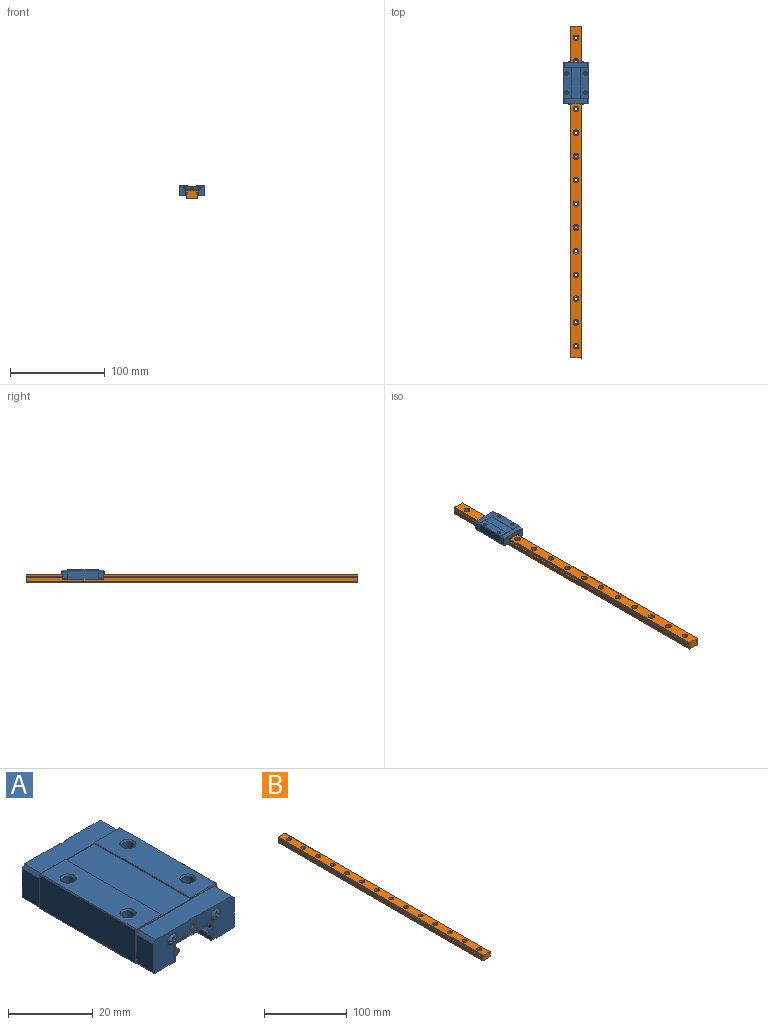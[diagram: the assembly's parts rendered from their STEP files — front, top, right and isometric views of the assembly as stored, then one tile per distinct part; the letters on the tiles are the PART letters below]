
ASSEMBLY  parts=2 mates=1
PART A: 286 faces, bbox 27.1x45.4x10.1 mm
  f0: plane 8.2x0.93mm, normal (0,-1,0), area 1.9mm2, adj f37,f39,f44,f244,f267
  f1: plane 8.2x0.93mm, normal (0,1,0), area 1.9mm2, adj f68,f70,f72,f141,f163
  f2: plane 3x3mm, normal (0,0,1), area 7.1mm2, adj f4
  f3: plane 3x3mm, normal (0,0,1), area 7.1mm2, adj f5
  f4: cylinder r=1.5mm len=5.45mm, axis (0,0,1), area 51.4mm2, adj f2,f31
  f5: cylinder r=1.5mm len=5.45mm, axis (0,0,1), area 51.4mm2, adj f3,f40
  f6: plane 8.2x0.93mm, normal (0,-1,0), area 1.9mm2, adj f26,f30,f33,f244,f266
  f7: plane 1.37x0.22mm, normal (0.71,-0.71,0), area 0.3mm2, adj f8,f50,f51,f186
  f8: cone r=1mm half-angle=45deg, axis (0,-1,0), area 1.1mm2, adj f7,f9,f10,f186
  f9: cylinder r=1mm len=32mm, axis (0,1,0), area 120.6mm2, adj f8,f11,f51,f59
  f10: plane 1.77x0.22mm, normal (0.71,-0.71,0), area 0.4mm2, adj f8,f11,f12,f186
  f11: plane 32x1.55mm, normal (1,0,0), area 49.6mm2, adj f9,f10,f13,f60
  f12: plane 12.4x0.2mm, normal (0,-0.71,-0.71), area 3.5mm2, adj f10,f13,f14,f186
  f13: plane 32x12mm, normal (0,0,-1), area 384mm2, adj f11,f12,f15,f61
  f14: plane 1.77x0.22mm, normal (-0.71,-0.71,0), area 0.4mm2, adj f12,f15,f16,f186
  f15: plane 32x1.55mm, normal (-1,0,0), area 49.6mm2, adj f13,f14,f17,f62
  f16: cone r=1.2mm half-angle=45deg, axis (0,-1,0), area 1.1mm2, adj f14,f17,f18,f186
  f17: cylinder r=1mm len=32mm, axis (0,1,0), area 120.6mm2, adj f15,f16,f19,f63
  f18: plane 1.37x0.22mm, normal (-0.71,-0.71,0), area 0.3mm2, adj f16,f19,f20,f186
  f19: plane 32x1.35mm, normal (-1,0,0), area 43.2mm2, adj f17,f18,f21,f64
  f20: plane 0.2x0.2mm, normal (-0.58,-0.58,-0.58), area 0mm2, adj f18,f21,f22
  f21: plane 32x0.2mm, normal (-0.71,0,-0.71), area 9.1mm2, adj f19,f20,f23,f65
  f22: plane 7.1x0.2mm, normal (0,-0.71,-0.71), area 2mm2, adj f20,f23,f24,f186
  f23: plane 32x7.1mm, normal (0,0,-1), area 227.2mm2, adj f21,f22,f25,f66
  f24: plane 0.2x0.2mm, normal (0.58,-0.58,-0.58), area 0mm2, adj f22,f25,f26
  f25: plane 32x0.2mm, normal (0.71,0,-0.71), area 9.1mm2, adj f23,f24,f27,f67
  f26: plane 9.6x0.2mm, normal (0.71,-0.71,0), area 2.7mm2, adj f6,f24,f27,f28,f185
  f27: plane 32x9.6mm, normal (1,0,0), area 307.2mm2, adj f25,f26,f29,f68
  f28: plane 0.2x0.2mm, normal (0.58,-0.58,0.58), area 0mm2, adj f26,f29,f30
  f29: plane 32x0.2mm, normal (0.71,0,0.71), area 9.1mm2, adj f27,f28,f32,f69
  f30: plane 8.4x0.2mm, normal (0,-0.71,0.71), area 2.3mm2, adj f6,f28,f32,f33
  f31: cone r=1.5mm half-angle=45deg, axis (0,0,1), area 6mm2, adj f4,f32
  f32: plane 32x8.4mm, normal (0,0,1), area 246.1mm2, adj f29,f30,f31,f34,f70,f71
  f33: plane 0.6x0.2mm, normal (-0.71,-0.71,0), area 0.1mm2, adj f6,f30,f34,f35,f184
  f34: plane 32x0.4mm, normal (-1,0,0), area 12.8mm2, adj f32,f33,f36,f72
  f35: plane 10.2x0.2mm, normal (0,-0.71,0.71), area 2.8mm2, adj f33,f36,f37,f184
  f36: plane 32x9.8mm, normal (0,0,1), area 313.6mm2, adj f34,f35,f38,f73
  f37: plane 0.6x0.2mm, normal (0.71,-0.71,0), area 0.1mm2, adj f0,f35,f38,f39,f184
  f38: plane 32x0.4mm, normal (1,0,0), area 12.8mm2, adj f36,f37,f41,f74
  f39: plane 8.4x0.2mm, normal (0,-0.71,0.71), area 2.3mm2, adj f0,f37,f41,f42
  f40: cone r=1.5mm half-angle=45deg, axis (0,0,1), area 6mm2, adj f5,f41
  f41: plane 32x8.4mm, normal (0,0,1), area 246.1mm2, adj f38,f39,f40,f43,f75,f76
  f42: plane 0.2x0.2mm, normal (-0.58,-0.58,0.58), area 0mm2, adj f39,f43,f44
  f43: plane 32x0.2mm, normal (-0.71,0,0.71), area 9.1mm2, adj f41,f42,f45,f77
  f44: plane 9.6x0.2mm, normal (-0.71,-0.71,0), area 2.7mm2, adj f0,f42,f45,f46,f187
  f45: plane 32x9.6mm, normal (-1,0,0), area 307.2mm2, adj f43,f44,f47,f78
  f46: plane 0.2x0.2mm, normal (-0.58,-0.58,-0.58), area 0mm2, adj f44,f47,f48
  f47: plane 32x0.2mm, normal (-0.71,0,-0.71), area 9.1mm2, adj f45,f46,f49,f79
  f48: plane 7.1x0.2mm, normal (0,-0.71,-0.71), area 2mm2, adj f46,f49,f50,f186
  f49: plane 32x7.1mm, normal (0,0,-1), area 227.2mm2, adj f47,f48,f52,f80
  f50: plane 0.2x0.2mm, normal (0.58,-0.58,-0.58), area 0mm2, adj f7,f48,f52
  f51: plane 32x1.35mm, normal (1,0,0), area 43.2mm2, adj f7,f9,f52,f58
  f52: plane 32x0.2mm, normal (0.71,0,-0.71), area 9.1mm2, adj f49,f50,f51,f81
  f53: plane 3x3mm, normal (0,0,1), area 7.1mm2, adj f55
  f54: plane 3x3mm, normal (0,0,1), area 7.1mm2, adj f56
  f55: cylinder r=1.5mm len=5.45mm, axis (0,0,1), area 51.4mm2, adj f53,f71
  f56: cylinder r=1.5mm len=5.45mm, axis (0,0,1), area 51.4mm2, adj f54,f76
  f57: plane 8.2x0.93mm, normal (0,1,0), area 1.9mm2, adj f74,f75,f78,f141,f164
  f58: plane 1.37x0.22mm, normal (0.71,0.71,0), area 0.3mm2, adj f51,f59,f81,f84
  f59: cone r=1mm half-angle=45deg, axis (0,1,0), area 1.1mm2, adj f9,f58,f60,f84
  f60: plane 1.77x0.22mm, normal (0.71,0.71,0), area 0.4mm2, adj f11,f59,f61,f84
  f61: plane 12.4x0.2mm, normal (0,0.71,-0.71), area 3.5mm2, adj f13,f60,f62,f84
  f62: plane 1.77x0.22mm, normal (-0.71,0.71,0), area 0.4mm2, adj f15,f61,f63,f84
  f63: cone r=1.2mm half-angle=45deg, axis (0,1,0), area 1.1mm2, adj f17,f62,f64,f84
  f64: plane 1.37x0.22mm, normal (-0.71,0.71,0), area 0.3mm2, adj f19,f63,f65,f84
  f65: plane 0.2x0.2mm, normal (-0.58,0.58,-0.58), area 0mm2, adj f21,f64,f66
  f66: plane 7.1x0.2mm, normal (0,0.71,-0.71), area 2mm2, adj f23,f65,f67,f84
  f67: plane 0.2x0.2mm, normal (0.58,0.58,-0.58), area 0mm2, adj f25,f66,f68
  f68: plane 9.6x0.2mm, normal (0.71,0.71,0), area 2.7mm2, adj f1,f27,f67,f69,f182
  f69: plane 0.2x0.2mm, normal (0.58,0.58,0.58), area 0mm2, adj f29,f68,f70
  f70: plane 8.4x0.2mm, normal (0,0.71,0.71), area 2.3mm2, adj f1,f32,f69,f72
  f71: cone r=1.5mm half-angle=45deg, axis (0,0,1), area 6mm2, adj f32,f55
  f72: plane 0.6x0.2mm, normal (-0.71,0.71,0), area 0.1mm2, adj f1,f34,f70,f73,f82
  f73: plane 10.2x0.2mm, normal (0,0.71,0.71), area 2.8mm2, adj f36,f72,f74,f82
  f74: plane 0.6x0.2mm, normal (0.71,0.71,0), area 0.1mm2, adj f38,f57,f73,f75,f82
  f75: plane 8.4x0.2mm, normal (0,0.71,0.71), area 2.3mm2, adj f41,f57,f74,f77
  f76: cone r=1.5mm half-angle=45deg, axis (0,0,1), area 6mm2, adj f41,f56
  f77: plane 0.2x0.2mm, normal (-0.58,0.58,0.58), area 0mm2, adj f43,f75,f78
  f78: plane 9.6x0.2mm, normal (-0.71,0.71,0), area 2.7mm2, adj f45,f57,f77,f79,f83
  f79: plane 0.2x0.2mm, normal (-0.58,0.58,-0.58), area 0mm2, adj f47,f78,f80
  f80: plane 7.1x0.2mm, normal (0,0.71,-0.71), area 2mm2, adj f49,f79,f81,f84
  f81: plane 0.2x0.2mm, normal (0.58,0.58,-0.58), area 0mm2, adj f52,f58,f80
  f82: plane 10.2x0.2mm, normal (0,-1,0), area 2mm2, adj f72,f73,f74,f141
  f83: plane 8.67x0.2mm, normal (0,-1,0), area 1.7mm2, adj f78,f146,f164,f165
  f84: plane 26.6x5.2mm, normal (0,-1,0), area 8mm2, adj f58,f59,f60,f61,f62,f63,f64,f66
  f85: sphere r=1.65mm, area 14.5mm2, adj f86,f87,f90,f92,f93,f96,f98,f99
  f86: plane 0.66x0.4mm, normal (0,0,-1), area 0.2mm2, adj f85,f87,f89,f90
  f87: plane 0.77x0.69mm, normal (-1,0,0), area 0.4mm2, adj f85,f86,f88,f108
  f88: plane 1.08x0.89mm, normal (-0.95,0.33,0), area 0.7mm2, adj f87,f89,f91,f109
  f89: plane 0.89x0.61mm, normal (0,0.33,-0.95), area 0.3mm2, adj f86,f88,f91
  f90: plane 0.77x0.69mm, normal (1,0,0), area 0.4mm2, adj f85,f86,f91,f96
  f91: plane 1.08x0.89mm, normal (0.95,0.33,0), area 0.7mm2, adj f88,f89,f90,f97
  f92: plane 0.61x0.35mm, normal (1,0,0), area 0.2mm2, adj f85,f93,f94,f96
  f93: plane 0.8x0.73mm, normal (0,0,1), area 0.4mm2, adj f85,f92,f95,f102
  f94: plane 0.89x0.61mm, normal (0.95,0.33,0), area 0.3mm2, adj f92,f95,f97
  f95: plane 1.08x0.89mm, normal (0,0.33,0.95), area 0.7mm2, adj f93,f94,f97,f103
  f96: plane 0.8x0.73mm, normal (0,0,-1), area 0.4mm2, adj f85,f90,f92,f97
  f97: plane 1.08x0.89mm, normal (0,0.33,-0.95), area 0.7mm2, adj f91,f94,f95,f96
  f98: plane 0.66x0.4mm, normal (0,0,1), area 0.2mm2, adj f85,f99,f100,f102
  f99: plane 0.77x0.69mm, normal (-1,0,0), area 0.4mm2, adj f85,f98,f101,f105
  f100: plane 0.89x0.61mm, normal (0,0.33,0.95), area 0.3mm2, adj f98,f101,f103
  f101: plane 1.08x0.89mm, normal (-0.95,0.33,0), area 0.7mm2, adj f99,f100,f103,f106
  f102: plane 0.77x0.69mm, normal (1,0,0), area 0.4mm2, adj f85,f93,f98,f103
  f103: plane 1.08x0.89mm, normal (0.95,0.33,0), area 0.7mm2, adj f95,f100,f101,f102
  f104: plane 0.61x0.35mm, normal (-1,0,0), area 0.2mm2, adj f85,f105,f107,f108
  f105: plane 0.8x0.73mm, normal (0,0,1), area 0.4mm2, adj f85,f99,f104,f106
  f106: plane 1.08x0.89mm, normal (0,0.33,0.95), area 0.7mm2, adj f101,f105,f107,f109
  f107: plane 0.89x0.61mm, normal (-0.95,0.33,0), area 0.3mm2, adj f104,f106,f109
  f108: plane 0.8x0.73mm, normal (0,0,-1), area 0.4mm2, adj f85,f87,f104,f109
  f109: plane 1.08x0.89mm, normal (0,0.33,-0.95), area 0.7mm2, adj f88,f106,f107,f108
  f110: sphere r=1.65mm, area 14.5mm2, adj f111,f112,f113,f117,f118,f120,f123,f124
  f111: plane 0.61x0.35mm, normal (-1,0,0), area 0.2mm2, adj f110,f112,f113,f114
  f112: plane 0.8x0.73mm, normal (0,0,-1), area 0.4mm2, adj f110,f111,f115,f125
  f113: plane 0.8x0.73mm, normal (0,0,1), area 0.4mm2, adj f110,f111,f116,f120
  f114: plane 0.89x0.61mm, normal (-0.95,0.33,0), area 0.3mm2, adj f111,f115,f116
  f115: plane 1.08x0.89mm, normal (0,0.33,-0.95), area 0.7mm2, adj f112,f114,f116,f128
  f116: plane 1.08x0.89mm, normal (0,0.33,0.95), area 0.7mm2, adj f113,f114,f115,f122
  f117: plane 0.66x0.4mm, normal (0,0,1), area 0.2mm2, adj f110,f118,f119,f120
  f118: plane 0.77x0.69mm, normal (1,0,0), area 0.4mm2, adj f110,f117,f121,f132
  f119: plane 0.89x0.61mm, normal (0,0.33,0.95), area 0.3mm2, adj f117,f121,f122
  f120: plane 0.77x0.69mm, normal (-1,0,0), area 0.4mm2, adj f110,f113,f117,f122
  f121: plane 1.08x0.89mm, normal (0.95,0.33,0), area 0.7mm2, adj f118,f119,f122,f134
  f122: plane 1.08x0.89mm, normal (-0.95,0.33,0), area 0.7mm2, adj f116,f119,f120,f121
  f123: plane 0.66x0.4mm, normal (0,0,-1), area 0.2mm2, adj f110,f124,f125,f126
  f124: plane 0.77x0.69mm, normal (1,0,0), area 0.4mm2, adj f110,f123,f127,f130
  f125: plane 0.77x0.69mm, normal (-1,0,0), area 0.4mm2, adj f110,f112,f123,f128
  f126: plane 0.89x0.61mm, normal (0,0.33,-0.95), area 0.3mm2, adj f123,f127,f128
  f127: plane 1.08x0.89mm, normal (0.95,0.33,0), area 0.7mm2, adj f124,f126,f128,f133
  f128: plane 1.08x0.89mm, normal (-0.95,0.33,0), area 0.7mm2, adj f115,f125,f126,f127
  f129: plane 0.61x0.35mm, normal (1,0,0), area 0.2mm2, adj f110,f130,f131,f132
  f130: plane 0.8x0.73mm, normal (0,0,-1), area 0.4mm2, adj f110,f124,f129,f133
  f131: plane 0.89x0.61mm, normal (0.95,0.33,0), area 0.3mm2, adj f129,f133,f134
  f132: plane 0.8x0.73mm, normal (0,0,1), area 0.4mm2, adj f110,f118,f129,f134
  f133: plane 1.08x0.89mm, normal (0,0.33,-0.95), area 0.7mm2, adj f127,f130,f131,f134
  f134: plane 1.08x0.89mm, normal (0,0.33,0.95), area 0.7mm2, adj f121,f131,f132,f133
  f135: plane 2.67x2mm, normal (0,-1,0), area 3.5mm2, adj f156,f157,f158,f159,f160,f180
  f136: plane 2.67x2mm, normal (0,-1,0), area 3.5mm2, adj f148,f149,f150,f151,f152,f181
  f137: plane 12.41x9.6mm, normal (0,1,0), area 77.5mm2, adj f139,f141,f142,f146,f164,f165,f169,f170
  f138: plane 12.41x9.6mm, normal (0,1,0), area 77.5mm2, adj f140,f141,f143,f162,f163,f166,f172,f173
  f139: plane 7.1x5.7mm, normal (0,0,-1), area 40.4mm2, adj f84,f137,f145,f147,f165,f167,f169,f177
  f140: plane 7.1x5.7mm, normal (0,0,-1), area 40.4mm2, adj f84,f138,f145,f161,f166,f174,f175,f178
  f141: plane 25.14x5.7mm, normal (0,0,1), area 142.9mm2, adj f1,f57,f82,f137,f138,f163,f164,f168
  f142: cylinder r=1.65mm len=3.3mm, axis (0,-1,0), area 9.1mm2, adj f110,f137,f167,f168,f169,f170
  f143: cylinder r=1.65mm len=3.3mm, axis (0,-1,0), area 9.1mm2, adj f85,f138,f168,f173,f174,f178
  f144: cylinder r=0.75mm len=1.5mm, axis (0,-1,0), area 3.3mm2, adj f168,f179
  f145: plane 12.8x5.36mm, normal (0,1,0), area 11.3mm2, adj f139,f140,f147,f148,f149,f150,f151,f152
  f146: plane 8.27x5.7mm, normal (-1,0,0), area 47.1mm2, adj f83,f137,f164,f165
  f147: plane 5.7x1.55mm, normal (1,0,0), area 8.8mm2, adj f84,f139,f145,f148,f181
  f148: cylinder r=1mm len=0.9mm, axis (0,-1,0), area 0.9mm2, adj f136,f145,f147,f149
  f149: plane 0.9x0.71mm, normal (0,0,-1), area 0.6mm2, adj f136,f145,f148,f150
  f150: plane 0.9x0.6mm, normal (1,0,0), area 0.5mm2, adj f136,f145,f149,f151
  f151: plane 0.9x0.71mm, normal (0,0,1), area 0.6mm2, adj f136,f145,f150,f152
  f152: cylinder r=1mm len=0.9mm, axis (0,-1,0), area 0.9mm2, adj f136,f145,f151,f153
  f153: plane 5.7x1.55mm, normal (1,0,0), area 8.8mm2, adj f84,f145,f152,f154,f181
  f154: plane 12x5.7mm, normal (0,0,-1), area 68.4mm2, adj f84,f145,f153,f155
  f155: plane 5.7x1.55mm, normal (-1,0,0), area 8.8mm2, adj f84,f145,f154,f156,f180
  f156: cylinder r=1mm len=0.9mm, axis (0,-1,0), area 0.9mm2, adj f135,f145,f155,f157
  f157: plane 0.9x0.71mm, normal (0,0,1), area 0.6mm2, adj f135,f145,f156,f158
  f158: plane 0.9x0.6mm, normal (-1,0,0), area 0.5mm2, adj f135,f145,f157,f159
  f159: plane 0.9x0.71mm, normal (0,0,-1), area 0.6mm2, adj f135,f145,f158,f160
  f160: cylinder r=1mm len=0.9mm, axis (0,-1,0), area 0.9mm2, adj f135,f145,f159,f161
  f161: plane 5.7x1.55mm, normal (-1,0,0), area 8.8mm2, adj f84,f140,f145,f160,f180
  f162: plane 8.27x5.7mm, normal (1,0,0), area 47.1mm2, adj f138,f163,f166,f182
  f163: plane 5.7x0.93mm, normal (0.71,0,0.71), area 7.5mm2, adj f1,f138,f141,f162,f182
  f164: plane 5.7x0.93mm, normal (-0.71,0,0.71), area 7.5mm2, adj f57,f83,f137,f141,f146
  f165: plane 5.7x0.4mm, normal (-0.71,0,-0.71), area 3.2mm2, adj f83,f84,f137,f139,f146
  f166: plane 5.7x0.4mm, normal (0.71,0,-0.71), area 3.2mm2, adj f84,f138,f140,f162,f182
  f167: plane 5.36x0.4mm, normal (0,1,0), area 2.1mm2, adj f139,f142,f169,f177
  f168: plane 12.8x4.24mm, normal (0,1,0), area 11.5mm2, adj f141,f142,f143,f144,f170,f171,f172,f173
  f169: plane 5.2x0.2mm, normal (1,0,0), area 1mm2, adj f137,f139,f142,f167
  f170: plane 4.83x0.2mm, normal (0,0,-1), area 1mm2, adj f137,f142,f168,f171
  f171: plane 3.84x0.2mm, normal (1,0,0), area 0.8mm2, adj f137,f141,f168,f170
  f172: plane 3.84x0.2mm, normal (-1,0,0), area 0.8mm2, adj f138,f141,f168,f173
  f173: plane 4.83x0.2mm, normal (0,0,-1), area 1mm2, adj f138,f143,f168,f172
  f174: plane 5.2x0.2mm, normal (-1,0,0), area 1mm2, adj f138,f140,f143,f178
  f175: plane 5.36x0.2mm, normal (1,0,0), area 1.1mm2, adj f140,f145,f176,f178
  f176: plane 12.8x0.2mm, normal (0,0,1), area 2.6mm2, adj f145,f168,f175,f177
  f177: plane 5.36x0.2mm, normal (-1,0,0), area 1.1mm2, adj f139,f145,f167,f176
  f178: plane 5.36x0.4mm, normal (0,1,0), area 2.1mm2, adj f140,f143,f174,f175
  f179: cylinder r=0.75mm len=4.8mm, axis (0,-1,0), area 22.6mm2, adj f144,f183
  f180: cylinder r=1mm len=4.8mm, axis (0,-1,0), area 18.1mm2, adj f84,f135,f155,f161
  f181: cylinder r=1mm len=4.8mm, axis (0,-1,0), area 18.1mm2, adj f84,f136,f147,f153
  f182: plane 8.67x0.2mm, normal (0,-1,0), area 1.7mm2, adj f68,f162,f163,f166
  f183: plane 1.5x1.5mm, normal (0,1,0), area 1.8mm2, adj f179
  f184: plane 10.2x0.2mm, normal (0,1,0), area 2mm2, adj f33,f35,f37,f244
  f185: plane 8.67x0.2mm, normal (0,1,0), area 1.7mm2, adj f26,f265,f266,f269
  f186: plane 26.6x5.2mm, normal (0,1,0), area 8mm2, adj f7,f8,f10,f12,f14,f16,f18,f22
  f187: plane 8.67x0.2mm, normal (0,1,0), area 1.7mm2, adj f44,f249,f267,f268
  f188: sphere r=1.65mm, area 14.5mm2, adj f189,f190,f193,f195,f196,f199,f201,f202
  f189: plane 0.66x0.4mm, normal (0,0,-1), area 0.2mm2, adj f188,f190,f192,f193
  f190: plane 0.77x0.69mm, normal (-1,0,0), area 0.4mm2, adj f188,f189,f191,f211
  f191: plane 1.08x0.89mm, normal (-0.95,-0.33,0), area 0.7mm2, adj f190,f192,f194,f212
  f192: plane 0.89x0.61mm, normal (0,-0.33,-0.95), area 0.3mm2, adj f189,f191,f194
  f193: plane 0.77x0.69mm, normal (1,0,0), area 0.4mm2, adj f188,f189,f194,f199
  f194: plane 1.08x0.89mm, normal (0.95,-0.33,0), area 0.7mm2, adj f191,f192,f193,f200
  f195: plane 0.61x0.35mm, normal (1,0,0), area 0.2mm2, adj f188,f196,f197,f199
  f196: plane 0.8x0.73mm, normal (0,0,1), area 0.4mm2, adj f188,f195,f198,f205
  f197: plane 0.89x0.61mm, normal (0.95,-0.33,0), area 0.3mm2, adj f195,f198,f200
  f198: plane 1.08x0.89mm, normal (0,-0.33,0.95), area 0.7mm2, adj f196,f197,f200,f206
  f199: plane 0.8x0.73mm, normal (0,0,-1), area 0.4mm2, adj f188,f193,f195,f200
  f200: plane 1.08x0.89mm, normal (0,-0.33,-0.95), area 0.7mm2, adj f194,f197,f198,f199
  f201: plane 0.66x0.4mm, normal (0,0,1), area 0.2mm2, adj f188,f202,f203,f205
  f202: plane 0.77x0.69mm, normal (-1,0,0), area 0.4mm2, adj f188,f201,f204,f208
  f203: plane 0.89x0.61mm, normal (0,-0.33,0.95), area 0.3mm2, adj f201,f204,f206
  f204: plane 1.08x0.89mm, normal (-0.95,-0.33,0), area 0.7mm2, adj f202,f203,f206,f209
  f205: plane 0.77x0.69mm, normal (1,0,0), area 0.4mm2, adj f188,f196,f201,f206
  f206: plane 1.08x0.89mm, normal (0.95,-0.33,0), area 0.7mm2, adj f198,f203,f204,f205
  f207: plane 0.61x0.35mm, normal (-1,0,0), area 0.2mm2, adj f188,f208,f210,f211
  f208: plane 0.8x0.73mm, normal (0,0,1), area 0.4mm2, adj f188,f202,f207,f209
  f209: plane 1.08x0.89mm, normal (0,-0.33,0.95), area 0.7mm2, adj f204,f208,f210,f212
  f210: plane 0.89x0.61mm, normal (-0.95,-0.33,0), area 0.3mm2, adj f207,f209,f212
  f211: plane 0.8x0.73mm, normal (0,0,-1), area 0.4mm2, adj f188,f190,f207,f212
  f212: plane 1.08x0.89mm, normal (0,-0.33,-0.95), area 0.7mm2, adj f191,f209,f210,f211
  f213: sphere r=1.65mm, area 14.5mm2, adj f214,f215,f216,f220,f221,f223,f226,f227
  f214: plane 0.61x0.35mm, normal (-1,0,0), area 0.2mm2, adj f213,f215,f216,f217
  f215: plane 0.8x0.73mm, normal (0,0,-1), area 0.4mm2, adj f213,f214,f218,f228
  f216: plane 0.8x0.73mm, normal (0,0,1), area 0.4mm2, adj f213,f214,f219,f223
  f217: plane 0.89x0.61mm, normal (-0.95,-0.33,0), area 0.3mm2, adj f214,f218,f219
  f218: plane 1.08x0.89mm, normal (0,-0.33,-0.95), area 0.7mm2, adj f215,f217,f219,f231
  f219: plane 1.08x0.89mm, normal (0,-0.33,0.95), area 0.7mm2, adj f216,f217,f218,f225
  f220: plane 0.66x0.4mm, normal (0,0,1), area 0.2mm2, adj f213,f221,f222,f223
  f221: plane 0.77x0.69mm, normal (1,0,0), area 0.4mm2, adj f213,f220,f224,f235
  f222: plane 0.89x0.61mm, normal (0,-0.33,0.95), area 0.3mm2, adj f220,f224,f225
  f223: plane 0.77x0.69mm, normal (-1,0,0), area 0.4mm2, adj f213,f216,f220,f225
  f224: plane 1.08x0.89mm, normal (0.95,-0.33,0), area 0.7mm2, adj f221,f222,f225,f237
  f225: plane 1.08x0.89mm, normal (-0.95,-0.33,0), area 0.7mm2, adj f219,f222,f223,f224
  f226: plane 0.66x0.4mm, normal (0,0,-1), area 0.2mm2, adj f213,f227,f228,f229
  f227: plane 0.77x0.69mm, normal (1,0,0), area 0.4mm2, adj f213,f226,f230,f233
  f228: plane 0.77x0.69mm, normal (-1,0,0), area 0.4mm2, adj f213,f215,f226,f231
  f229: plane 0.89x0.61mm, normal (0,-0.33,-0.95), area 0.3mm2, adj f226,f230,f231
  f230: plane 1.08x0.89mm, normal (0.95,-0.33,0), area 0.7mm2, adj f227,f229,f231,f236
  f231: plane 1.08x0.89mm, normal (-0.95,-0.33,0), area 0.7mm2, adj f218,f228,f229,f230
  f232: plane 0.61x0.35mm, normal (1,0,0), area 0.2mm2, adj f213,f233,f234,f235
  f233: plane 0.8x0.73mm, normal (0,0,-1), area 0.4mm2, adj f213,f227,f232,f236
  f234: plane 0.89x0.61mm, normal (0.95,-0.33,0), area 0.3mm2, adj f232,f236,f237
  f235: plane 0.8x0.73mm, normal (0,0,1), area 0.4mm2, adj f213,f221,f232,f237
  f236: plane 1.08x0.89mm, normal (0,-0.33,-0.95), area 0.7mm2, adj f230,f233,f234,f237
  f237: plane 1.08x0.89mm, normal (0,-0.33,0.95), area 0.7mm2, adj f224,f234,f235,f236
  f238: plane 2.67x2mm, normal (0,1,0), area 3.5mm2, adj f251,f252,f253,f254,f255,f284
  f239: plane 2.67x2mm, normal (0,1,0), area 3.5mm2, adj f259,f260,f261,f262,f263,f283
  f240: plane 12.41x9.6mm, normal (0,-1,0), area 77.5mm2, adj f242,f244,f245,f249,f267,f268,f272,f273
  f241: plane 12.41x9.6mm, normal (0,-1,0), area 77.5mm2, adj f243,f244,f246,f265,f266,f269,f275,f276
  f242: plane 7.1x5.7mm, normal (0,0,-1), area 40.4mm2, adj f186,f240,f248,f250,f268,f270,f272,f280
  f243: plane 7.1x5.7mm, normal (0,0,-1), area 40.4mm2, adj f186,f241,f248,f264,f269,f277,f278,f281
  f244: plane 25.14x5.7mm, normal (0,0,1), area 142.9mm2, adj f0,f6,f184,f240,f241,f266,f267,f271
  f245: cylinder r=1.65mm len=3.3mm, axis (0,1,0), area 9.1mm2, adj f213,f240,f270,f271,f272,f273
  f246: cylinder r=1.65mm len=3.3mm, axis (0,1,0), area 9.1mm2, adj f188,f241,f271,f276,f277,f281
  f247: cylinder r=0.75mm len=1.5mm, axis (0,1,0), area 3.3mm2, adj f271,f282
  f248: plane 12.8x5.36mm, normal (0,-1,0), area 11.3mm2, adj f242,f243,f250,f251,f252,f253,f254,f255
  f249: plane 8.27x5.7mm, normal (-1,0,0), area 47.1mm2, adj f187,f240,f267,f268
  f250: plane 5.7x1.55mm, normal (1,0,0), area 8.8mm2, adj f186,f242,f248,f251,f284
  f251: cylinder r=1mm len=0.9mm, axis (0,1,0), area 0.9mm2, adj f238,f248,f250,f252
  f252: plane 0.9x0.71mm, normal (0,0,-1), area 0.6mm2, adj f238,f248,f251,f253
  f253: plane 0.9x0.6mm, normal (1,0,0), area 0.5mm2, adj f238,f248,f252,f254
  f254: plane 0.9x0.71mm, normal (0,0,1), area 0.6mm2, adj f238,f248,f253,f255
  f255: cylinder r=1mm len=0.9mm, axis (0,1,0), area 0.9mm2, adj f238,f248,f254,f256
  f256: plane 5.7x1.55mm, normal (1,0,0), area 8.8mm2, adj f186,f248,f255,f257,f284
  f257: plane 12x5.7mm, normal (0,0,-1), area 68.4mm2, adj f186,f248,f256,f258
  f258: plane 5.7x1.55mm, normal (-1,0,0), area 8.8mm2, adj f186,f248,f257,f259,f283
  f259: cylinder r=1mm len=0.9mm, axis (0,1,0), area 0.9mm2, adj f239,f248,f258,f260
  f260: plane 0.9x0.71mm, normal (0,0,1), area 0.6mm2, adj f239,f248,f259,f261
  f261: plane 0.9x0.6mm, normal (-1,0,0), area 0.5mm2, adj f239,f248,f260,f262
  f262: plane 0.9x0.71mm, normal (0,0,-1), area 0.6mm2, adj f239,f248,f261,f263
  f263: cylinder r=1mm len=0.9mm, axis (0,1,0), area 0.9mm2, adj f239,f248,f262,f264
  f264: plane 5.7x1.55mm, normal (-1,0,0), area 8.8mm2, adj f186,f243,f248,f263,f283
  f265: plane 8.27x5.7mm, normal (1,0,0), area 47.1mm2, adj f185,f241,f266,f269
  f266: plane 5.7x0.93mm, normal (0.71,0,0.71), area 7.5mm2, adj f6,f185,f241,f244,f265
  f267: plane 5.7x0.93mm, normal (-0.71,0,0.71), area 7.5mm2, adj f0,f187,f240,f244,f249
  f268: plane 5.7x0.4mm, normal (-0.71,0,-0.71), area 3.2mm2, adj f186,f187,f240,f242,f249
  f269: plane 5.7x0.4mm, normal (0.71,0,-0.71), area 3.2mm2, adj f185,f186,f241,f243,f265
  f270: plane 5.36x0.4mm, normal (0,-1,0), area 2.1mm2, adj f242,f245,f272,f280
  f271: plane 12.8x4.24mm, normal (0,-1,0), area 11.5mm2, adj f244,f245,f246,f247,f273,f274,f275,f276
  f272: plane 5.2x0.2mm, normal (1,0,0), area 1mm2, adj f240,f242,f245,f270
  f273: plane 4.83x0.2mm, normal (0,0,-1), area 1mm2, adj f240,f245,f271,f274
  f274: plane 3.84x0.2mm, normal (1,0,0), area 0.8mm2, adj f240,f244,f271,f273
  f275: plane 3.84x0.2mm, normal (-1,0,0), area 0.8mm2, adj f241,f244,f271,f276
  f276: plane 4.83x0.2mm, normal (0,0,-1), area 1mm2, adj f241,f246,f271,f275
  f277: plane 5.2x0.2mm, normal (-1,0,0), area 1mm2, adj f241,f243,f246,f281
  f278: plane 5.36x0.2mm, normal (1,0,0), area 1.1mm2, adj f243,f248,f279,f281
  f279: plane 12.8x0.2mm, normal (0,0,1), area 2.6mm2, adj f248,f271,f278,f280
  f280: plane 5.36x0.2mm, normal (-1,0,0), area 1.1mm2, adj f242,f248,f270,f279
  f281: plane 5.36x0.4mm, normal (0,-1,0), area 2.1mm2, adj f243,f246,f277,f278
  f282: cylinder r=0.75mm len=4.8mm, axis (0,1,0), area 22.6mm2, adj f247,f285
  f283: cylinder r=1mm len=4.8mm, axis (0,1,0), area 18.1mm2, adj f186,f239,f258,f264
  f284: cylinder r=1mm len=4.8mm, axis (0,1,0), area 18.1mm2, adj f186,f238,f250,f256
  f285: plane 1.5x1.5mm, normal (0,-1,0), area 1.8mm2, adj f282
PART B: 64 faces, bbox 12x350x8 mm
  f0: plane 350x1.25mm, normal (-1,0,0), area 437.1mm2, adj f1,f19,f20,f51
  f1: cylinder r=1mm len=350mm, axis (0,1,0), area 333.8mm2, adj f0,f2,f20,f51
  f2: plane 350x0.71mm, normal (0,0,-1), area 248.9mm2, adj f1,f3,f20,f51
  f3: plane 350x0.6mm, normal (-1,0,0), area 208.6mm2, adj f2,f4,f20,f51
  f4: plane 350x0.71mm, normal (0,0,1), area 248.9mm2, adj f3,f5,f20,f51
  f5: cylinder r=1mm len=350mm, axis (0,1,0), area 333.8mm2, adj f4,f6,f20,f51
  f6: plane 350x4.25mm, normal (-1,0,0), area 1487.1mm2, adj f5,f7,f20,f51
  f7: plane 350x0.3mm, normal (-0.71,0,-0.71), area 148.5mm2, adj f6,f8,f20,f51
  f8: plane 350x11.4mm, normal (0,0,-1), area 3855.3mm2, adj f7,f9,f20,f23,f42,f43,f44,f45
  f9: plane 350x0.3mm, normal (0.71,0,-0.71), area 148.5mm2, adj f8,f10,f20,f51
  f10: plane 350x4.25mm, normal (1,0,0), area 1487.1mm2, adj f9,f11,f20,f51
  f11: cylinder r=1mm len=350mm, axis (0,1,0), area 333.8mm2, adj f10,f12,f20,f51
  f12: plane 350x0.71mm, normal (0,0,1), area 248.9mm2, adj f11,f13,f20,f51
  f13: plane 350x0.6mm, normal (1,0,0), area 208.6mm2, adj f12,f14,f20,f51
  f14: plane 350x0.71mm, normal (0,0,-1), area 248.9mm2, adj f13,f15,f20,f51
  f15: cylinder r=1mm len=350mm, axis (0,1,0), area 333.8mm2, adj f14,f16,f20,f51
  f16: plane 350x1.25mm, normal (1,0,0), area 437.1mm2, adj f15,f17,f20,f51
  f17: plane 350x0.3mm, normal (0.71,0,0.71), area 148.5mm2, adj f16,f18,f20,f51
  f18: plane 350x11.4mm, normal (0,0,1), area 3594.2mm2, adj f17,f19,f20,f21,f24,f27,f29,f31
  f19: plane 350x0.3mm, normal (-0.71,0,0.71), area 148.5mm2, adj f0,f18,f20,f51
  f20: plane 12x8mm, normal (0,1,0), area 93.1mm2, adj f0,f1,f2,f3,f4,f5,f6,f7
  f21: cylinder r=3mm len=6mm, axis (0,0,1), area 84.8mm2, adj f18,f22
  f22: plane 6x6mm, normal (0,0,1), area 18.7mm2, adj f21,f23
  f23: cylinder r=1.75mm len=3.5mm, axis (0,0,1), area 38.5mm2, adj f8,f22
  f24: cylinder r=3mm len=6mm, axis (0,0,1), area 84.8mm2, adj f18,f25
  f25: plane 6x6mm, normal (0,0,1), area 18.7mm2, adj f24,f42
  f26: plane 6x6mm, normal (0,0,1), area 18.7mm2, adj f27,f43
  f27: cylinder r=3mm len=6mm, axis (0,0,1), area 84.8mm2, adj f18,f26
  f28: plane 6x6mm, normal (0,0,1), area 18.7mm2, adj f29,f44
  f29: cylinder r=3mm len=6mm, axis (0,0,1), area 84.8mm2, adj f18,f28
  f30: plane 6x6mm, normal (0,0,1), area 18.7mm2, adj f31,f45
  f31: cylinder r=3mm len=6mm, axis (0,0,1), area 84.8mm2, adj f18,f30
  f32: plane 6x6mm, normal (0,0,1), area 18.7mm2, adj f33,f46
  f33: cylinder r=3mm len=6mm, axis (0,0,1), area 84.8mm2, adj f18,f32
  f34: plane 6x6mm, normal (0,0,1), area 18.7mm2, adj f35,f47
  f35: cylinder r=3mm len=6mm, axis (0,0,1), area 84.8mm2, adj f18,f34
  f36: plane 6x6mm, normal (0,0,1), area 18.7mm2, adj f37,f48
  f37: cylinder r=3mm len=6mm, axis (0,0,1), area 84.8mm2, adj f18,f36
  f38: plane 6x6mm, normal (0,0,1), area 18.7mm2, adj f39,f49
  f39: cylinder r=3mm len=6mm, axis (0,0,1), area 84.8mm2, adj f18,f38
  f40: plane 6x6mm, normal (0,0,1), area 18.7mm2, adj f41,f50
  f41: cylinder r=3mm len=6mm, axis (0,0,1), area 84.8mm2, adj f18,f40
  f42: cylinder r=1.75mm len=3.5mm, axis (0,0,1), area 38.5mm2, adj f8,f25
  f43: cylinder r=1.75mm len=3.5mm, axis (0,0,1), area 38.5mm2, adj f8,f26
  f44: cylinder r=1.75mm len=3.5mm, axis (0,0,1), area 38.5mm2, adj f8,f28
  f45: cylinder r=1.75mm len=3.5mm, axis (0,0,1), area 38.5mm2, adj f8,f30
  f46: cylinder r=1.75mm len=3.5mm, axis (0,0,1), area 38.5mm2, adj f8,f32
  f47: cylinder r=1.75mm len=3.5mm, axis (0,0,1), area 38.5mm2, adj f8,f34
  f48: cylinder r=1.75mm len=3.5mm, axis (0,0,1), area 38.5mm2, adj f8,f36
  f49: cylinder r=1.75mm len=3.5mm, axis (0,0,1), area 38.5mm2, adj f8,f38
  f50: cylinder r=1.75mm len=3.5mm, axis (0,0,1), area 38.5mm2, adj f8,f40
  f51: plane 12x8mm, normal (0,-1,0), area 93.1mm2, adj f0,f1,f2,f3,f4,f5,f6,f7
  f52: cylinder r=3mm len=6mm, axis (0,0,1), area 75.4mm2, adj f18,f53
  f53: plane 6x6mm, normal (0,0,1), area 18.7mm2, adj f52,f63
  f54: cylinder r=3mm len=6mm, axis (0,0,1), area 75.4mm2, adj f18,f55
  f55: plane 6x6mm, normal (0,0,1), area 18.7mm2, adj f54,f62
  f56: cylinder r=3mm len=6mm, axis (0,0,1), area 75.4mm2, adj f18,f57
  f57: plane 6x6mm, normal (0,0,1), area 18.7mm2, adj f56,f61
  f58: cylinder r=3mm len=6mm, axis (0,0,1), area 75.4mm2, adj f18,f59
  f59: plane 6x6mm, normal (0,0,1), area 18.7mm2, adj f58,f60
  f60: cylinder r=1.75mm len=4mm, axis (0,0,1), area 44mm2, adj f8,f59
  f61: cylinder r=1.75mm len=4mm, axis (0,0,1), area 44mm2, adj f8,f57
  f62: cylinder r=1.75mm len=4mm, axis (0,0,1), area 44mm2, adj f8,f55
  f63: cylinder r=1.75mm len=4mm, axis (0,0,1), area 44mm2, adj f8,f53
PLACE A t=(-0.12,135.35,4.86)mm
PLACE B rot(axis=(0,1,0),0deg) t=(-0.12,195.41,0.86)mm fixed
MATE slider B.f51 <-> A.f271  axis (0,-1,0) through (-0.12,-154.59,0.81)mm
